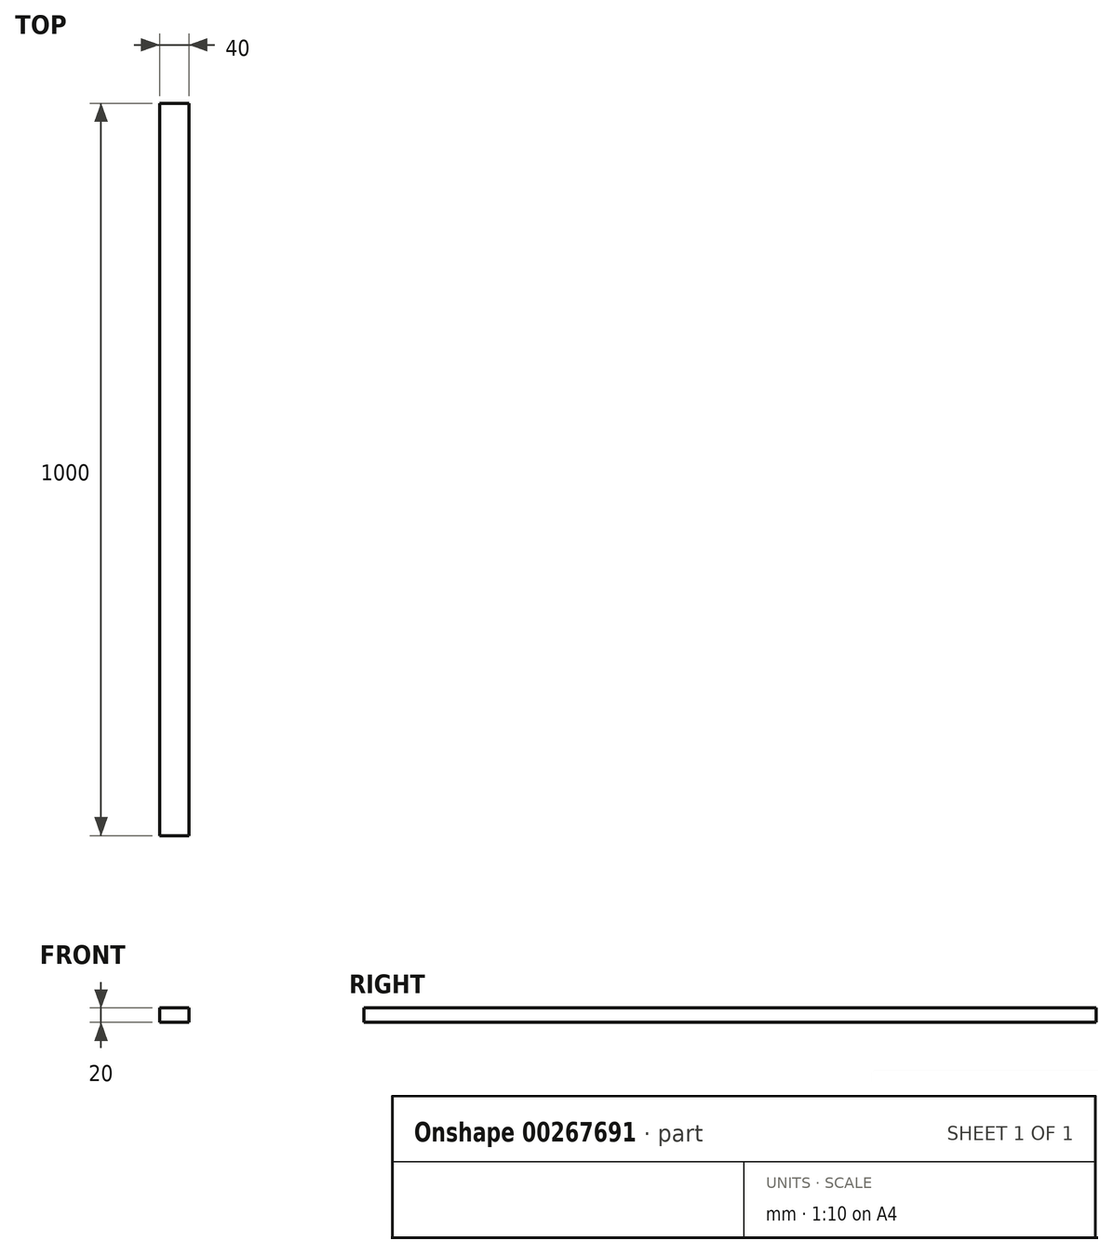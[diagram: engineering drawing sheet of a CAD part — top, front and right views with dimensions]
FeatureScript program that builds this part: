
annotation { "Feature Type Name" : "Feature", "Feature Type Description" : "" }
export const myFeature = defineFeature(function(context is Context, id is Id, definition is map)
    precondition{}
    {
        {
            var Q0;
            Q0=qCreatedBy(makeId("Front.planeOp"),FACE);
            var sketch = newSketch(context, id + "F0", { "sketchPlane" : qUnion([Q0])});
            skLineSegment(sketch, "E0.bottom", {"start": v(20, 10) * mm, "end": v(-20, 10) * mm});
            skLineSegment(sketch, "E0.top", {"start": v(20, -10) * mm, "end": v(-20, -10) * mm});
            skLineSegment(sketch, "E0.left", {"start": v(20, 10) * mm, "end": v(20, -10) * mm});
            skLineSegment(sketch, "E0.right", {"start": v(-20, 10) * mm, "end": v(-20, -10) * mm});
            skPoint(sketch, "E0.middle", {"position": v(0, 0) * mm});
            skSolve(sketch);
        }
        {
            var Q0;
            Q0=makeQuery(id+"F0.imprint","IMPRINT",FACE,{"disambiguationData":[TD([[makeQuery(id+"F0.imprint","IMPRINT",EDGE,{"derivedFrom":sQuery(id+"F0.wireOp",EDGE,"E0.bottom")}),1.0]])]});
            extrude(context, id + "F1", {"entities" : qUnion([Q0]), "oppositeDirection" : true, "depth" : 1000 * mm});
        }
    });
